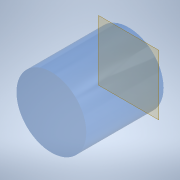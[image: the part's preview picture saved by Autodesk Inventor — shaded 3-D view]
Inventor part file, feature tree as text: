
AUTODESK INVENTOR PART (.ipt)
format: ipt  version: 2021 (Build 250183000, 183)  size: 161,280 bytes
history: native  units: mm
features: other x4, extrude x3, fillet x3, sketch x3, reference x2
ambient origin geometry x8: Origin, YZ Plane, XZ Plane, XY Plane, X Axis, Y Axis, Z Axis, Center Point
bodies: Body1 (feature_tree)
feature tree (15):
  other  "Bryła1"
  other  "Płaszczyzna konstrukcyjna1"
  extrude  "Wyciągnięcie proste1"  Depth=310.0mm TaperAngle=0.0deg
  fillet  "Zaokrąglenie1"  Radius=30.0mm
  extrude  "Wyciągnięcie proste2"  Depth=160.0mm
  fillet  "Zaokrąglenie2"  Radius=30.0mm
  fillet  "Zaokrąglenie3"  Radius=30.0mm
  extrude  "Wyciągnięcie proste3"  Depth=20.0mm
  sketch  "Szkic1"
  reference  "Odniesienie1"
  reference  "Odniesienie2"
  sketch  "Szkic2"
  sketch  "Szkic3"
  other  "wszystko.iam"
  other  "garnek:1"
